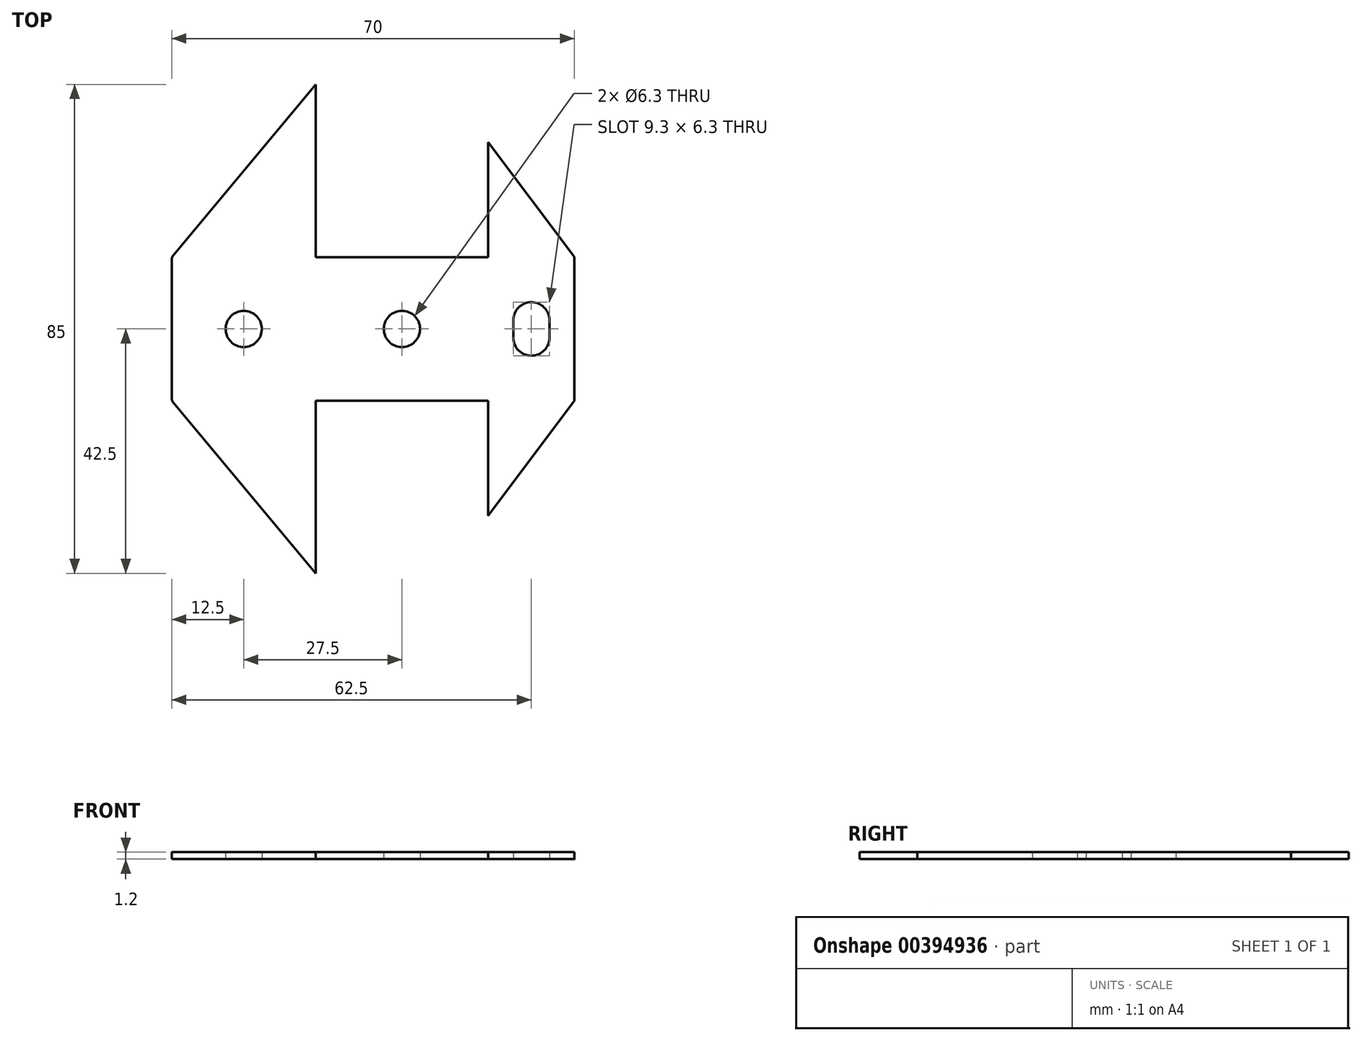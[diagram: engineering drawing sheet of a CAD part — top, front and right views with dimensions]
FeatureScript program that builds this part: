
annotation { "Feature Type Name" : "Feature", "Feature Type Description" : "" }
export const myFeature = defineFeature(function(context is Context, id is Id, definition is map)
    precondition{}
    {
        {
            var Q0;
            Q0=qCreatedBy(makeId("Top.planeOp"),FACE);
            var sketch = newSketch(context, id + "F0", { "sketchPlane" : qUnion([Q0])});
            skLineSegment(sketch, "E0.bottom", {"start": v(0, 0) * mm, "end": v(70, 0) * mm});
            skLineSegment(sketch, "E0.top", {"start": v(0, 25) * mm, "end": v(70, 25) * mm});
            skLineSegment(sketch, "E0.left", {"start": v(0, 0) * mm, "end": v(0, 25) * mm});
            skLineSegment(sketch, "E0.right", {"start": v(70, 0) * mm, "end": v(70, 25) * mm});
            skLineSegment(sketch, "E1", {"start": v(62.5, 25) * mm, "end": v(62.5, 0) * mm, "construction": true});
            skArc(sketch, "E2", {"start": v(59.35, 11) * mm, "mid": v(62.5, 7.85) * mm, "end": v(65.65, 11) * mm});
            skArc(sketch, "E3", {"start": v(65.65, 14) * mm, "mid": v(62.5, 17.15) * mm, "end": v(59.35, 14) * mm});
            skLineSegment(sketch, "E4", {"start": v(65.65, 14) * mm, "end": v(65.65, 11) * mm});
            skLineSegment(sketch, "E5", {"start": v(59.35, 14) * mm, "end": v(59.35, 11) * mm});
            skLineSegment(sketch, "E6", {"start": v(0, 25) * mm, "end": v(25, 55) * mm});
            skLineSegment(sketch, "E7", {"start": v(25, 55) * mm, "end": v(25, 25) * mm});
            skLineSegment(sketch, "E8", {"start": v(0, 0) * mm, "end": v(25, -30) * mm});
            skLineSegment(sketch, "E9", {"start": v(25, -30) * mm, "end": v(25, 0) * mm});
            skLineSegment(sketch, "E10", {"start": v(70, 25) * mm, "end": v(55, 45) * mm});
            skLineSegment(sketch, "E11", {"start": v(55, 45) * mm, "end": v(55, 25) * mm});
            skLineSegment(sketch, "E12", {"start": v(70, 0) * mm, "end": v(55, -20) * mm});
            skLineSegment(sketch, "E13", {"start": v(55, -20) * mm, "end": v(55, 0) * mm});
            skLineSegment(sketch, "E14", {"start": v(0, 25) * mm, "end": v(25, 0) * mm, "construction": true});
            skLineSegment(sketch, "E15", {"start": v(0, 0) * mm, "end": v(25, 25) * mm, "construction": true});
            skPoint(sketch, "E16", {"position": v(12.5, 12.5) * mm});
            skCircle(sketch, "E17", {"center": v(12.5, 12.5) * mm, "radius": 3.15 * mm});
            skLineSegment(sketch, "E18", {"start": v(25, 25) * mm, "end": v(55, 0) * mm, "construction": true});
            skLineSegment(sketch, "E19", {"start": v(25, 0) * mm, "end": v(55, 25) * mm, "construction": true});
            skCircle(sketch, "E20", {"center": v(40, 12.5) * mm, "radius": 3.15 * mm});
            skSolve(sketch);
        }
        {
            var Q0;
            Q0 = qSketchRegion(id + "F0", true);
            extrude(context, id + "F1", {"entities" : qUnion([Q0]), "depth" : 1.2 * mm});
        }
        {
            var Q0;
            Q0=makeQuery(id+"F1.opExtrude","SWEPT_EDGE",EDGE,{"disambiguationData":[OSD([sQuery(id+"F0.wireOp",EDGE,"E0.top"),sQuery(id+"F0.wireOp",EDGE,"E0.left"),sQuery(id+"F0.wireOp",EDGE,"E6")])]});
            var Q1;
            Q1=makeQuery(id+"F1.opExtrude","SWEPT_EDGE",EDGE,{"disambiguationData":[OSD([sQuery(id+"F0.wireOp",EDGE,"E0.bottom"),sQuery(id+"F0.wireOp",EDGE,"E0.left"),sQuery(id+"F0.wireOp",EDGE,"E8")])]});
            var Q2;
            Q2=makeQuery(id+"F1.opExtrude","SWEPT_EDGE",EDGE,{"disambiguationData":[OSD([sQuery(id+"F0.wireOp",EDGE,"E0.bottom"),sQuery(id+"F0.wireOp",EDGE,"E0.right"),sQuery(id+"F0.wireOp",EDGE,"E12")])]});
            var Q3;
            Q3=makeQuery(id+"F1.opExtrude","SWEPT_EDGE",EDGE,{"disambiguationData":[OSD([sQuery(id+"F0.wireOp",EDGE,"E0.top"),sQuery(id+"F0.wireOp",EDGE,"E0.right"),sQuery(id+"F0.wireOp",EDGE,"E10")])]});
            fillet(context, id + "F2", {"entities" : qUnion([Q0, Q1, Q2, Q3]), "radius" : 1 * mm, "tangentPropagation" : true, "allowEdgeOverflow" : false});
        }
    });
